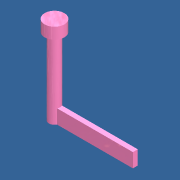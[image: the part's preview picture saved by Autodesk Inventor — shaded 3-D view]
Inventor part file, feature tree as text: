
AUTODESK INVENTOR PART (.ipt)
format: ipt  version: 2020 (Build 240168000, 168)  size: 134,656 bytes
history: native  units: mm
features: extrude x4, sketch x4
ambient origin geometry x8: Origin, YZ Plane, XZ Plane, XY Plane, X Axis, Y Axis, Z Axis, Center Point
bodies: Solid1 (feature_tree)
feature tree (8):
  extrude  "Extrusion1"  Depth=54.5mm TaperAngle=0.0deg
  extrude  "Extrusion2"  Depth=8.0mm TaperAngle=0.0deg
  extrude  "Extrusion3"  Depth=11.0mm
  extrude  "Extrusion10"  Depth=8.0mm
  sketch  "Sketch1"  dims[d0=8.0mm d1=54.5mm d2=0.0mm]
  sketch  "Sketch2"  dims[d3=14.0mm d4=8.0mm d5=0.0mm]
  sketch  "Sketch3"  dims[d6=56.0mm d7=11.0mm]
  sketch  "Sketch12"  dims[d8=3.5mm d9=0.0mm d41=8.0mm d42=56.0mm d43=0.0mm]
